# Revit family: Lavatory-TOTO-Contemporary-Luminist-LLT152
name_source: partatom
category: Plumbing Fixtures
revit_build: Autodesk Revit Architecture 2013 (Build: 20130531_2115(x64)
units: mm (PartAtom-declared; Revit-internal decimal feet)

## types (1)
- LLT152
    04 CSI = 22 42 16
    95 CSI = 15410
    ADA Compliant = Yes
    Assembly Code = D2010310
    Basin Depth = 3 1/2"
    Basin Diameter = 0"
    CAD Drawing URL = http://assets.totousa.com
    Certifications = IAPMO(cUPC), State of Massachusetts, and others
    Code Compliance = UPC, IPC, NSPC, NPC Canada, and others
    Cold Water Connection Radius = 3/16"
    Cold Water Connector = Cold Water Connection
    Color Availability = #63 Angelic White
    Default Elevation = 48"
    Depth = 15 5/8"
    Description = Lloyd® Metal Console Lavatory
    Diameter = 15 5/8"
    Finish = Vitreous China - TOTO - 01 Cotton
    Height = 0"
    Hot Water Connection Radius = 3/16"
    Hot Water Connector = Hot Water Connection
    Industry Standards = Meets and exceeds CSA B45 series, ANSI Z124.3, UL 1951, CSA 22.2 14
    Manufacturer = TOTO USA, Inc.
    Manufacturer Fax = (770) 282-0002
    Material = Epoxy Resin
    Model = LLT152
    Sanitary Connector = Sanitary Connection
    Series = Luminist
    Shipping Weight = 19.00 lb
    Spec Sheet URL = http://assets.totousa.com
    Style = Contemporary
    Subcategory = Lavatories
    Toto BIM Number = BM-00334
    URL = http://www.totousa.com
    Warranty = One Year Limited Warranty
    Warranty URL = http://www.totousa.com
    Waste Connection NPT Radius = 5/8"
    Width = 24"

## geometry (parser evidence)
native form markers: Blend x16, Sweep x3
no freeform markers — native parametric forms only
